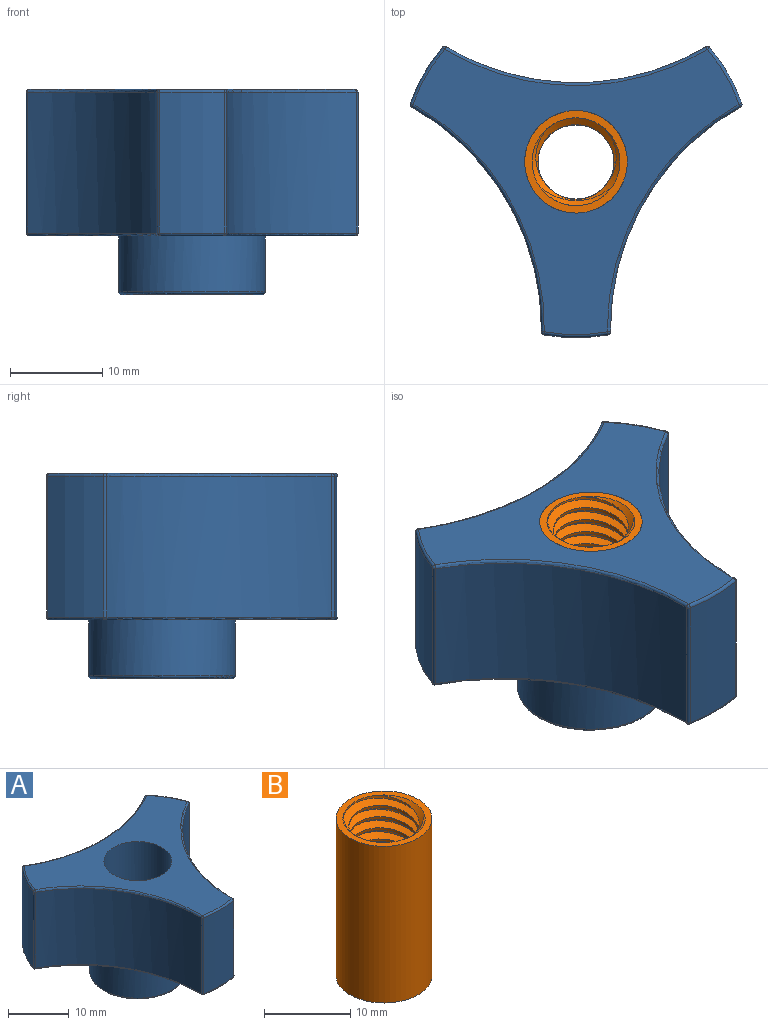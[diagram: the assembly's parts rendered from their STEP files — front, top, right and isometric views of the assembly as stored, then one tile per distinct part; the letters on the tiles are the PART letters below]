
ASSEMBLY  parts=2 mates=1
PART A: 42 faces, bbox 36.5x32x22.2 mm
  f0: sphere r=0.32mm, area 0.1mm2, adj f4,f5,f6
  f1: sphere r=0.32mm, area 0.1mm2, adj f7,f8,f9
  f2: sphere r=0.32mm, area 0.1mm2, adj f4,f9,f10
  f3: cylinder r=5.56mm len=22.23mm, axis (0,0,1), area 775.9mm2, adj f11,f14
  f4: torus R=18.73mm, axis (0,0,-1), area 3.5mm2, adj f0,f2,f14,f16
  f5: torus R=27.75mm, axis (0,0,-1), area 14.8mm2, adj f0,f14,f15,f17
  f6: cylinder r=0.32mm len=15.24mm, axis (0,0,1), area 6.8mm2, adj f0,f16,f17,f18
  f7: torus R=18.73mm, axis (0,0,-1), area 3.5mm2, adj f1,f13,f14,f20
  f8: cylinder r=0.32mm len=15.24mm, axis (0,0,1), area 6.8mm2, adj f1,f20,f21,f23
  f9: torus R=27.75mm, axis (0,0,-1), area 14.8mm2, adj f1,f2,f14,f23
  f10: cylinder r=0.32mm len=15.24mm, axis (0,0,-1), area 6.8mm2, adj f2,f16,f22,f23
  f11: plane 15.52x15.24mm, normal (0,0,-1), area 85.4mm2, adj f3,f24
  f12: cylinder r=0.32mm len=15.24mm, axis (0,0,-1), area 6.8mm2, adj f13,f19,f20,f34
  f13: sphere r=0.32mm, area 0.1mm2, adj f7,f12,f25
  f14: plane 35.33x30.93mm, normal (0,0,1), area 390.3mm2, adj f3,f4,f5,f7,f9,f25,f26
  f15: sphere r=0.32mm, area 0.1mm2, adj f5,f26,f27
  f16: cylinder r=19.05mm len=15.24mm, axis (0,0,1), area 107.1mm2, adj f4,f6,f10,f28
  f17: cylinder r=27.43mm len=28.14mm, axis (0,0,1), area 450.2mm2, adj f5,f6,f27,f29
  f18: sphere r=0.32mm, area 0.1mm2, adj f6,f28,f29
  f19: sphere r=0.32mm, area 0.1mm2, adj f12,f30,f33
  f20: cylinder r=19.05mm len=15.24mm, axis (0,0,1), area 107.1mm2, adj f7,f8,f12,f30
  f21: sphere r=0.32mm, area 0.1mm2, adj f8,f30,f31
  f22: sphere r=0.32mm, area 0.1mm2, adj f10,f28,f31
  f23: cylinder r=27.43mm len=24.37mm, axis (0,0,1), area 450.2mm2, adj f8,f9,f10,f31
  f24: torus R=7.62mm, axis (0,0,1), area 24.5mm2, adj f11,f32
  f25: torus R=27.75mm, axis (0,0,-1), area 14.8mm2, adj f13,f14,f34,f35
  f26: torus R=18.73mm, axis (0,0,-1), area 3.5mm2, adj f14,f15,f35,f36
  f27: cylinder r=0.32mm len=15.24mm, axis (0,0,-1), area 6.8mm2, adj f15,f17,f36,f37
  f28: torus R=18.73mm, axis (0,0,1), area 3.5mm2, adj f16,f18,f22,f38
  f29: torus R=27.75mm, axis (0,0,1), area 14.8mm2, adj f17,f18,f37,f38
  f30: torus R=18.73mm, axis (0,0,1), area 3.5mm2, adj f19,f20,f21,f38
  f31: torus R=27.75mm, axis (0,0,1), area 14.8mm2, adj f21,f22,f23,f38
  f32: cylinder r=7.94mm len=15.88mm, axis (0,0,1), area 300.9mm2, adj f24,f38
  f33: torus R=27.75mm, axis (0,0,1), area 14.8mm2, adj f19,f34,f38,f41
  f34: cylinder r=27.43mm len=24.37mm, axis (0,0,1), area 450.2mm2, adj f12,f25,f33,f39
  f35: sphere r=0.32mm, area 0.1mm2, adj f25,f26,f39
  f36: cylinder r=19.05mm len=15.24mm, axis (0,0,1), area 107.1mm2, adj f26,f27,f39,f40
  f37: sphere r=0.32mm, area 0.1mm2, adj f27,f29,f40
  f38: plane 35.33x30.93mm, normal (0,0,-1), area 289.3mm2, adj f28,f29,f30,f31,f32,f33,f40
  f39: cylinder r=0.32mm len=15.24mm, axis (0,0,1), area 6.8mm2, adj f34,f35,f36,f41
  f40: torus R=18.73mm, axis (0,0,1), area 3.5mm2, adj f36,f37,f38,f41
  f41: sphere r=0.32mm, area 0.1mm2, adj f33,f39,f40
PART B: 67 faces, bbox 11.1x11.3x22.8 mm
  f0: cylinder r=4.12mm len=8.24mm, axis (0,-0.16,0.99), area 10.3mm2, adj f1,f2
  f1: cone r=4.12mm half-angle=60deg, axis (0,0.16,-0.99), area 23.4mm2, adj f0,f3
  f2: cone r=4.98mm half-angle=60deg, axis (0,-0.16,0.99), area 23.4mm2, adj f0,f4
  f3: cylinder r=4.76mm len=9.53mm, axis (0,0,-1), area 11.5mm2, adj f1,f5
  f4: cylinder r=4.76mm len=9.53mm, axis (0,0,-1), area 11.6mm2, adj f2,f6
  f5: cone r=4.98mm half-angle=60deg, axis (0,-0.16,0.99), area 23.4mm2, adj f3,f7
  f6: cone r=4.12mm half-angle=60deg, axis (0,0.16,-0.99), area 23.4mm2, adj f4,f8
  f7: cylinder r=4.12mm len=8.24mm, axis (0,-0.16,0.99), area 10.3mm2, adj f5,f9
  f8: cylinder r=4.12mm len=8.24mm, axis (0,-0.16,0.99), area 10.3mm2, adj f6,f10
  f9: cone r=4.12mm half-angle=60deg, axis (0,0.16,-0.99), area 23.4mm2, adj f7,f11
  f10: cone r=4.98mm half-angle=60deg, axis (0,-0.16,0.99), area 23.4mm2, adj f8,f12
  f11: cylinder r=4.76mm len=9.53mm, axis (0,0,-1), area 11.5mm2, adj f9,f13
  f12: cylinder r=4.76mm len=9.53mm, axis (0,0,-1), area 11.6mm2, adj f10,f14
  f13: cone r=4.98mm half-angle=60deg, axis (0,-0.16,0.99), area 23.4mm2, adj f11,f15
  f14: cone r=4.12mm half-angle=60deg, axis (0,0.16,-0.99), area 23.4mm2, adj f12,f16
  f15: cylinder r=4.12mm len=8.24mm, axis (0,-0.16,0.99), area 10.3mm2, adj f13,f17
  f16: cylinder r=4.12mm len=8.24mm, axis (0,-0.16,0.99), area 10.3mm2, adj f14,f18
  f17: cone r=4.12mm half-angle=60deg, axis (0,0.16,-0.99), area 23.4mm2, adj f15,f19
  f18: cone r=4.98mm half-angle=60deg, axis (0,-0.16,0.99), area 23.4mm2, adj f16,f20
  f19: cylinder r=4.76mm len=9.53mm, axis (0,0,-1), area 11.5mm2, adj f17,f21
  f20: cylinder r=4.76mm len=9.53mm, axis (0,0,-1), area 11.4mm2, adj f18,f22
  f21: cone r=4.98mm half-angle=60deg, axis (0,-0.16,0.99), area 23.4mm2, adj f19,f23
  f22: cone r=4.12mm half-angle=60deg, axis (0,0.16,-0.99), area 23.4mm2, adj f20,f24
  f23: cylinder r=4.12mm len=8.24mm, axis (0,-0.16,0.99), area 10.3mm2, adj f21,f25
  f24: cylinder r=4.12mm len=8.24mm, axis (0,-0.16,0.99), area 10.3mm2, adj f22,f26
  f25: cone r=4.12mm half-angle=60deg, axis (0,0.16,-0.99), area 23.4mm2, adj f23,f27
  f26: cone r=4.98mm half-angle=60deg, axis (0,-0.16,0.99), area 23.4mm2, adj f24,f28
  f27: cylinder r=4.76mm len=9.53mm, axis (0,0,-1), area 11.5mm2, adj f25,f29
  f28: cylinder r=4.76mm len=9.53mm, axis (0,0,-1), area 11.4mm2, adj f26,f30
  f29: cone r=4.98mm half-angle=60deg, axis (0,-0.16,0.99), area 23.4mm2, adj f27,f31
  f30: cone r=4.12mm half-angle=60deg, axis (0,0.16,-0.99), area 23.4mm2, adj f28,f32
  f31: cylinder r=4.12mm len=8.24mm, axis (0,-0.16,0.99), area 10.3mm2, adj f29,f33
  f32: cylinder r=4.12mm len=8.24mm, axis (0,-0.16,0.99), area 10.3mm2, adj f30,f34
  f33: cone r=4.12mm half-angle=60deg, axis (0,0.16,-0.99), area 23.4mm2, adj f31,f35
  f34: cone r=4.98mm half-angle=60deg, axis (0,-0.16,0.99), area 23.4mm2, adj f32,f36
  f35: cylinder r=4.76mm len=9.53mm, axis (0,0,-1), area 11.5mm2, adj f33,f37
  f36: cylinder r=4.76mm len=9.53mm, axis (0,0,-1), area 11.4mm2, adj f34,f38
  f37: cone r=4.98mm half-angle=60deg, axis (0,-0.16,0.99), area 23.4mm2, adj f35,f39
  f38: cone r=4.12mm half-angle=60deg, axis (0,0.16,-0.99), area 23.4mm2, adj f36,f40
  f39: cylinder r=4.12mm len=8.24mm, axis (0,-0.16,0.99), area 10.3mm2, adj f37,f41
  f40: cylinder r=4.12mm len=8.24mm, axis (0,-0.16,0.99), area 10.3mm2, adj f38,f42
  f41: cone r=4.12mm half-angle=60deg, axis (0,0.16,-0.99), area 23.4mm2, adj f39,f43
  f42: cone r=4.98mm half-angle=60deg, axis (0,-0.16,0.99), area 23.4mm2, adj f40,f44
  f43: cylinder r=4.76mm len=9.53mm, axis (0,0,-1), area 11.5mm2, adj f41,f45
  f44: cylinder r=4.76mm len=9.53mm, axis (0,0,-1), area 11.5mm2, adj f42,f46
  f45: cone r=4.98mm half-angle=60deg, axis (0,-0.16,0.99), area 23.4mm2, adj f43,f49
  f46: cone r=4.12mm half-angle=60deg, axis (0,0.16,-0.99), area 23.4mm2, adj f44,f52
  f47: cone r=4.12mm half-angle=60deg, axis (0,0.16,-0.99), area 0.5mm2, adj f53,f54
  f48: cylinder r=4.12mm len=2.62mm, axis (0,-0.16,0.99), area 0mm2, adj f50,f54
  f49: cylinder r=4.12mm len=8.24mm, axis (0,-0.16,0.99), area 10mm2, adj f45,f51,f55
  f50: cone r=4.98mm half-angle=60deg, axis (0,-0.16,0.99), area 10.4mm2, adj f48,f54,f56
  f51: cone r=4.12mm half-angle=60deg, axis (0,0.16,-0.99), area 20.9mm2, adj f49,f55,f56
  f52: cylinder r=4.12mm len=8.24mm, axis (0,-0.16,0.99), area 10.3mm2, adj f46,f57
  f53: cylinder r=4.76mm len=5.07mm, axis (0,0,-1), area 0.3mm2, adj f47,f58
  f54: cone r=4.76mm half-angle=45deg, axis (0,0,-1), area 10.8mm2, adj f47,f48,f50,f58
  f55: cone r=4.76mm half-angle=45deg, axis (0,0,-1), area 3.2mm2, adj f49,f51,f58
  f56: cylinder r=4.76mm len=9.53mm, axis (0,0,-1), area 11.2mm2, adj f50,f51,f58
  f57: cone r=4.98mm half-angle=60deg, axis (0,-0.16,0.99), area 23.4mm2, adj f52,f59
  f58: plane 11.32x11.11mm, normal (0,0,-1), area 25.7mm2, adj f53,f54,f55,f56,f60
  f59: cylinder r=4.76mm len=9.53mm, axis (0,0,-1), area 11.1mm2, adj f57,f62,f63
  f60: cylinder r=5.56mm len=22.23mm, axis (0,0,-1), area 775.9mm2, adj f58,f63
  f61: cylinder r=4.76mm len=7.86mm, axis (0,0,-1), area 1.6mm2, adj f63,f64
  f62: cone r=4.12mm half-angle=60deg, axis (0,0.16,-0.99), area 14.3mm2, adj f59,f65,f66
  f63: plane 11.32x11.11mm, normal (0,0,1), area 25.7mm2, adj f59,f60,f61,f66
  f64: cone r=4.98mm half-angle=60deg, axis (0,-0.16,0.99), area 2.6mm2, adj f61,f66
  f65: cylinder r=4.12mm len=6.88mm, axis (0,-0.16,0.99), area 1.2mm2, adj f62,f66
  f66: cone r=3.97mm half-angle=45deg, axis (0,0,1), area 12mm2, adj f62,f63,f64,f65
PLACE A t=(0,0,11.11)mm
PLACE B t=(0,0,11.11)mm
MATE fastened B.f60 <-> A.f3  axis (0,0,-1) through (0,0,0)mm
